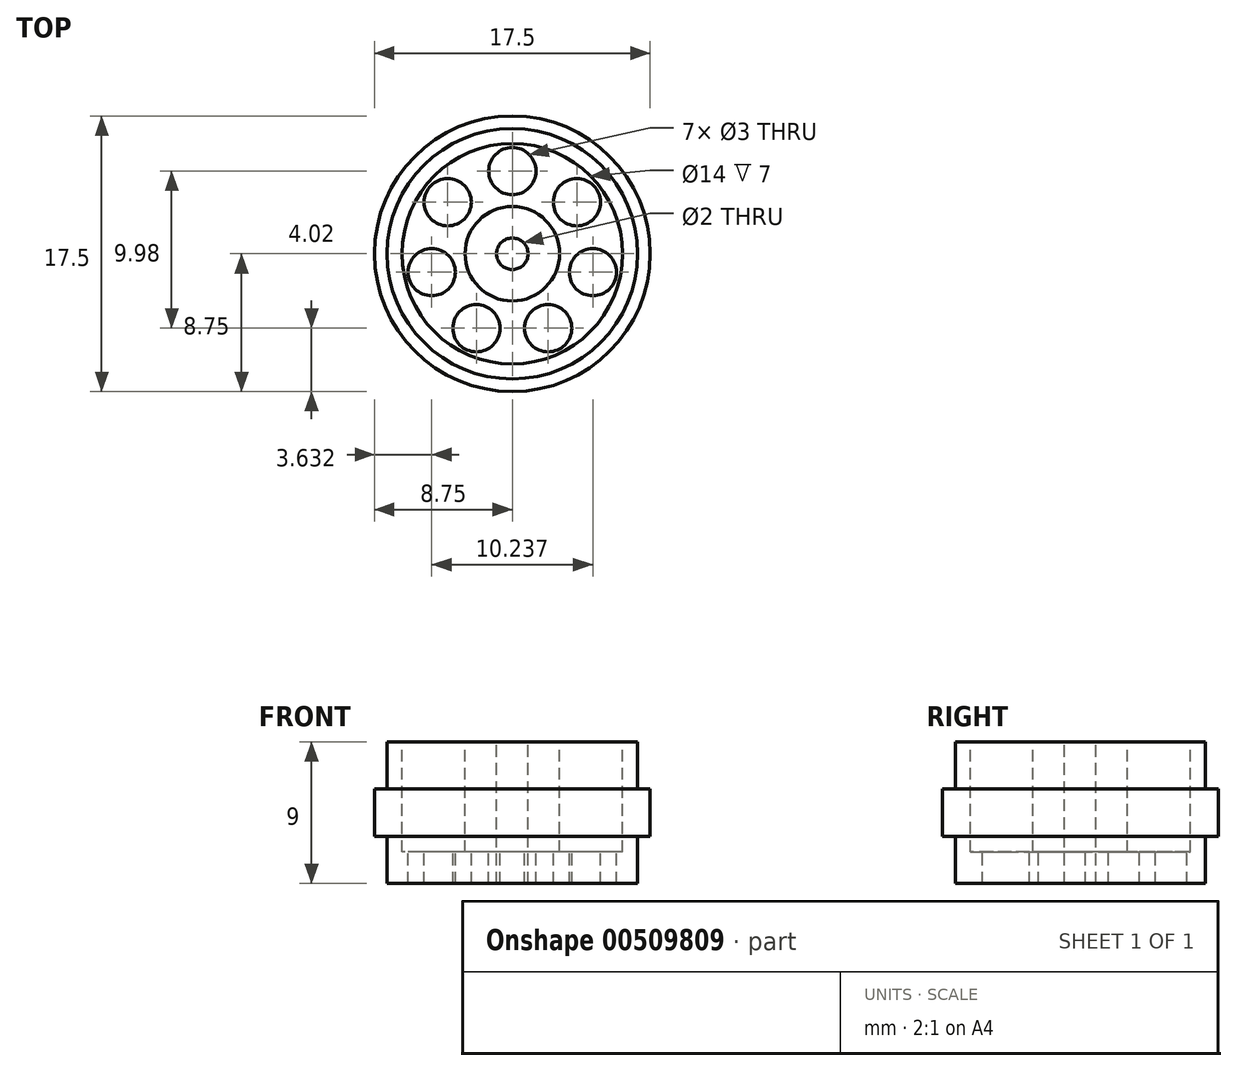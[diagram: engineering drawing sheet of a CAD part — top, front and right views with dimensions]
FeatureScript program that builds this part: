
annotation { "Feature Type Name" : "Feature", "Feature Type Description" : "" }
export const myFeature = defineFeature(function(context is Context, id is Id, definition is map)
    precondition{}
    {
        {
            var Q0;
            Q0=qCreatedBy(makeId("Top.planeOp"),FACE);
            var sketch = newSketch(context, id + "F0", { "sketchPlane" : qUnion([Q0])});
            skCircle(sketch, "E0", {"center": v(0, 0) * mm, "radius": 7.95 * mm});
            skSolve(sketch);
        }
        {
            var Q0;
            Q0=makeQuery(id+"F0.imprint","IMPRINT",FACE,{"disambiguationData":[TD([[makeQuery(id+"F0.imprint","IMPRINT",EDGE,{"derivedFrom":sQuery(id+"F0.wireOp",EDGE,"E0")}),1.0]])]});
            extrude(context, id + "F1", {"entities" : qUnion([Q0]), "depth" : 3 * mm, "offsetDistance" : 25 * mm});
        }
        {
            var Q0;
            Q0=makeQuery(id+"F1.opExtrude","CAP_FACE",FACE,{"disambiguationData":[OSD([sQuery(id+"F0.wireOp",EDGE,"E0")])],"isStart":false});
            var sketch = newSketch(context, id + "F2", { "sketchPlane" : qUnion([Q0])});
            skCircle(sketch, "E1", {"center": v(0, 0) * mm, "radius": 8.75 * mm});
            skSolve(sketch);
        }
        {
            var Q0;
            Q0=makeQuery(id+"F2.imprint","IMPRINT",FACE,{"disambiguationData":[TD([[makeQuery(id+"F2.imprint","IMPRINT",EDGE,{"derivedFrom":sQuery(id+"F2.wireOp",EDGE,"E1")}),1.0]])]});
            var Q1;
            Q1=makeQuery(id+"F2.imprint","IMPRINT",FACE,{"disambiguationData":[TD([[makeQuery(id+"F2.imprint","IMPRINT",EDGE,{"derivedFrom":makeQuery(id+"F1.opExtrude","CAP_EDGE",EDGE,{"disambiguationData":[OSD([sQuery(id+"F0.wireOp",EDGE,"E0")])],"isStart":false})}),1.0]])]});
            extrude(context, id + "F3", {"entities" : qUnion([Q0, Q1]), "operationType" : NewBodyOperationType.ADD, "depth" : 3 * mm, "offsetDistance" : 25 * mm});
        }
        {
            var Q0;
            Q0=makeQuery(id+"F3.opExtrude","CAP_FACE",FACE,{"disambiguationData":[OSD([sQuery(id+"F2.wireOp",EDGE,"E1")])],"isStart":false});
            var sketch = newSketch(context, id + "F4", { "sketchPlane" : qUnion([Q0])});
            skCircle(sketch, "E2", {"center": v(0, 0) * mm, "radius": 7.95 * mm});
            skSolve(sketch);
        }
        {
            var Q0;
            Q0=makeQuery(id+"F4.imprint","IMPRINT",FACE,{"disambiguationData":[TD([[makeQuery(id+"F4.imprint","IMPRINT",EDGE,{"derivedFrom":sQuery(id+"F4.wireOp",EDGE,"E2")}),1.0]])]});
            extrude(context, id + "F5", {"entities" : qUnion([Q0]), "operationType" : NewBodyOperationType.ADD, "depth" : 3 * mm, "offsetDistance" : 25 * mm});
        }
        {
            var Q0;
            Q0=makeQuery(id+"F5.opExtrude","CAP_FACE",FACE,{"disambiguationData":[OSD([sQuery(id+"F4.wireOp",EDGE,"E2")])],"isStart":false});
            var sketch = newSketch(context, id + "F6", { "sketchPlane" : qUnion([Q0])});
            skCircle(sketch, "E3", {"center": v(0, 0) * mm, "radius": 5.25 * mm, "construction": true});
            skCircle(sketch, "E4", {"center": v(0, 5.25) * mm, "radius": 1.5 * mm});
            skCircle(sketch, "E5.1.0", {"center": v(-4.1, 3.27) * mm, "radius": 1.5 * mm});
            skCircle(sketch, "E5.2.0", {"center": v(-5.12, -1.17) * mm, "radius": 1.5 * mm});
            skCircle(sketch, "E5.3.0", {"center": v(-2.28, -4.73) * mm, "radius": 1.5 * mm});
            skCircle(sketch, "E5.4.0", {"center": v(2.28, -4.73) * mm, "radius": 1.5 * mm});
            skCircle(sketch, "E5.5.0", {"center": v(5.12, -1.17) * mm, "radius": 1.5 * mm});
            skCircle(sketch, "E5.6.0", {"center": v(4.1, 3.27) * mm, "radius": 1.5 * mm});
            skSolve(sketch);
        }
        {
            var Q0;
            Q0=makeQuery(id+"F6.imprint","IMPRINT",FACE,{"disambiguationData":[TD([[makeQuery(id+"F6.imprint","IMPRINT",EDGE,{"derivedFrom":sQuery(id+"F6.wireOp",EDGE,"E5.1.0")}),1.0]])]});
            var Q1;
            Q1=makeQuery(id+"F6.imprint","IMPRINT",FACE,{"disambiguationData":[TD([[makeQuery(id+"F6.imprint","IMPRINT",EDGE,{"derivedFrom":sQuery(id+"F6.wireOp",EDGE,"E4")}),1.0]])]});
            var Q2;
            Q2=makeQuery(id+"F6.imprint","IMPRINT",FACE,{"disambiguationData":[TD([[makeQuery(id+"F6.imprint","IMPRINT",EDGE,{"derivedFrom":sQuery(id+"F6.wireOp",EDGE,"E5.6.0")}),1.0]])]});
            var Q3;
            Q3=makeQuery(id+"F6.imprint","IMPRINT",FACE,{"disambiguationData":[TD([[makeQuery(id+"F6.imprint","IMPRINT",EDGE,{"derivedFrom":sQuery(id+"F6.wireOp",EDGE,"E5.5.0")}),1.0]])]});
            var Q4;
            Q4=makeQuery(id+"F6.imprint","IMPRINT",FACE,{"disambiguationData":[TD([[makeQuery(id+"F6.imprint","IMPRINT",EDGE,{"derivedFrom":sQuery(id+"F6.wireOp",EDGE,"E5.4.0")}),1.0]])]});
            var Q5;
            Q5=makeQuery(id+"F6.imprint","IMPRINT",FACE,{"disambiguationData":[TD([[makeQuery(id+"F6.imprint","IMPRINT",EDGE,{"derivedFrom":sQuery(id+"F6.wireOp",EDGE,"E5.3.0")}),1.0]])]});
            var Q6;
            Q6=makeQuery(id+"F6.imprint","IMPRINT",FACE,{"disambiguationData":[TD([[makeQuery(id+"F6.imprint","IMPRINT",EDGE,{"derivedFrom":sQuery(id+"F6.wireOp",EDGE,"E5.2.0")}),1.0]])]});
            extrude(context, id + "F7", {"entities" : qUnion([Q0, Q1, Q2, Q3, Q4, Q5, Q6]), "operationType" : NewBodyOperationType.REMOVE, "oppositeDirection" : true, "depth" : 25 * mm, "offsetDistance" : 25 * mm});
        }
        {
            var Q0;
            Q0=makeQuery(id+"F5.opExtrude","CAP_FACE",FACE,{"disambiguationData":[OSD([sQuery(id+"F4.wireOp",EDGE,"E2")])],"isStart":false});
            var sketch = newSketch(context, id + "F8", { "sketchPlane" : qUnion([Q0])});
            skCircle(sketch, "E6", {"center": v(0, 0) * mm, "radius": 7 * mm});
            skCircle(sketch, "E7", {"center": v(0, 0) * mm, "radius": 3 * mm});
            skCircle(sketch, "E8", {"center": v(0, 0) * mm, "radius": 1 * mm});
            skSolve(sketch);
        }
        {
            var Q0;
            Q0=makeQuery(id+"F8.imprint","IMPRINT",FACE,{"disambiguationData":[TD([[makeQuery(id+"F8.imprint","IMPRINT",EDGE,{"derivedFrom":sQuery(id+"F8.wireOp",EDGE,"E6")}),1.0]])]});
            extrude(context, id + "F9", {"entities" : qUnion([Q0]), "operationType" : NewBodyOperationType.REMOVE, "oppositeDirection" : true, "depth" : 7 * mm, "offsetDistance" : 25 * mm});
        }
        {
            var Q0;
            Q0=makeQuery(id+"F9.boolean.opBoolean","SPLIT",FACE,{"disambiguationData":[TD([makeQuery(id+"F9.opExtrude","SWEPT_FACE",FACE,{"disambiguationData":[OSD([sQuery(id+"F8.wireOp",EDGE,"E7")])]})])],"derivedFrom":makeQuery(id+"F5.opExtrude","CAP_FACE",FACE,{"disambiguationData":[OSD([sQuery(id+"F4.wireOp",EDGE,"E2")])],"isStart":false})});
            var sketch = newSketch(context, id + "F10", { "sketchPlane" : qUnion([Q0])});
            skCircle(sketch, "E9", {"center": v(0, 0) * mm, "radius": 1 * mm});
            skSolve(sketch);
        }
        {
            var Q0;
            Q0=makeQuery(id+"F10.imprint","IMPRINT",FACE,{"disambiguationData":[TD([[makeQuery(id+"F10.imprint","IMPRINT",EDGE,{"derivedFrom":sQuery(id+"F10.wireOp",EDGE,"E9")}),1.0]])]});
            extrude(context, id + "F11", {"entities" : qUnion([Q0]), "operationType" : NewBodyOperationType.REMOVE, "oppositeDirection" : true, "depth" : 25 * mm, "offsetDistance" : 25 * mm});
        }
    });
